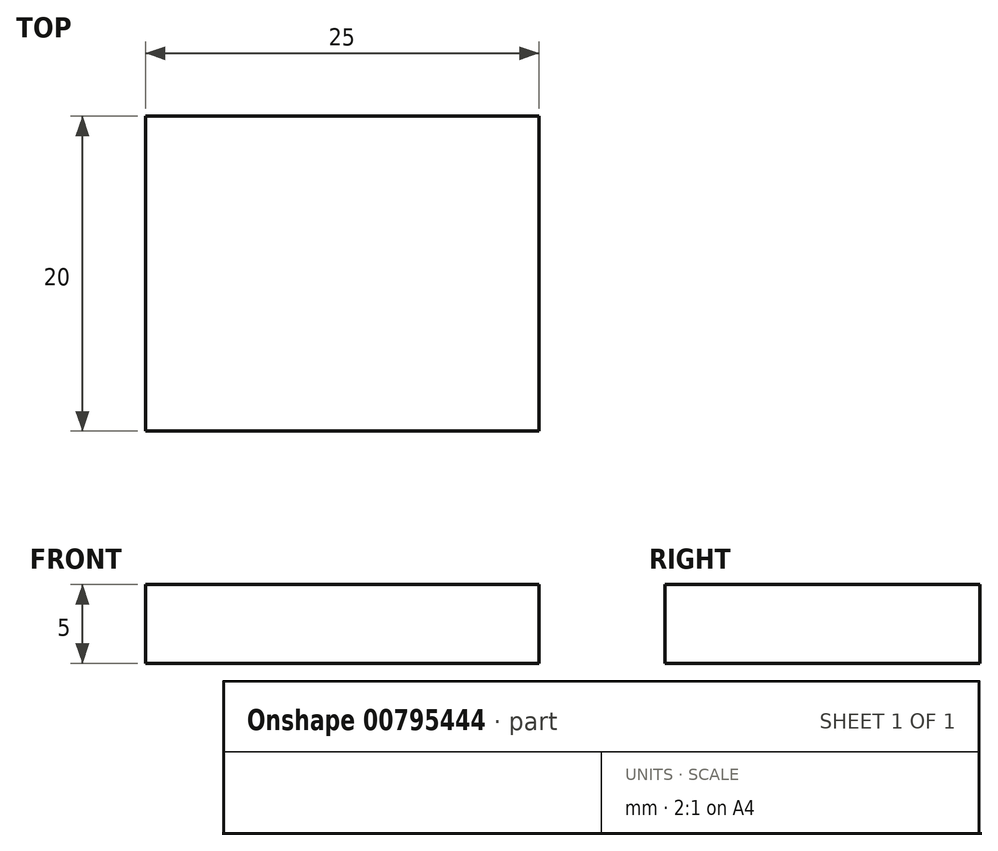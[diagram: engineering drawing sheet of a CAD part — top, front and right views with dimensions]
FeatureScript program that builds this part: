
annotation { "Feature Type Name" : "Feature", "Feature Type Description" : "" }
export const myFeature = defineFeature(function(context is Context, id is Id, definition is map)
    precondition{}
    {
        {
            var Q0;
            Q0=qCreatedBy(makeId("Right.planeOp"),FACE);
            var sketch = newSketch(context, id + "F0", { "sketchPlane" : qUnion([Q0])});
            skLineSegment(sketch, "E0.bottom", {"start": v(-21.56, 6.06) * mm, "end": v(-1.56, 6.06) * mm});
            skLineSegment(sketch, "E0.top", {"start": v(-21.56, 1.06) * mm, "end": v(-1.56, 1.06) * mm});
            skLineSegment(sketch, "E0.left", {"start": v(-21.56, 6.06) * mm, "end": v(-21.56, 1.06) * mm});
            skLineSegment(sketch, "E0.right", {"start": v(-1.56, 6.06) * mm, "end": v(-1.56, 1.06) * mm});
            skSolve(sketch);
        }
        {
            var Q0;
            Q0=makeQuery(id+"F0.imprint","IMPRINT",FACE,{"disambiguationData":[TD([[makeQuery(id+"F0.imprint","IMPRINT",EDGE,{"derivedFrom":sQuery(id+"F0.wireOp",EDGE,"E0.bottom")}),-1.0]])]});
            extrude(context, id + "F1", {"entities" : qUnion([Q0]), "depth" : 25 * mm, "offsetDistance" : 25 * mm});
        }
    });
